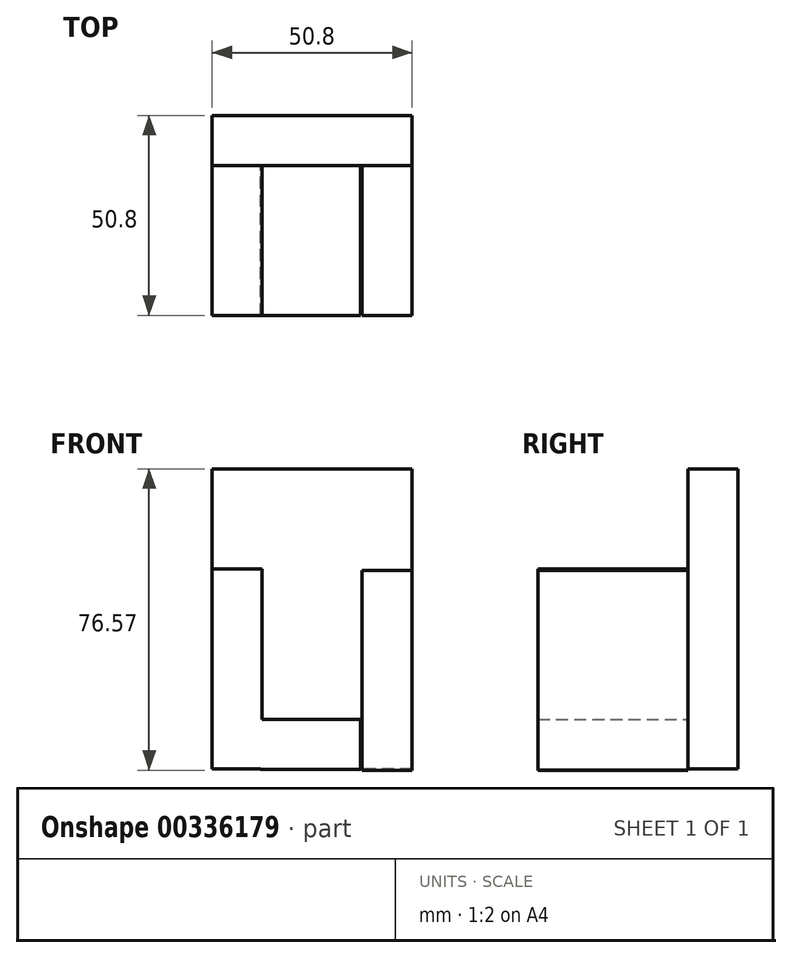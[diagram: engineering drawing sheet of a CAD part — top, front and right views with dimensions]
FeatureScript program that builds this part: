
annotation { "Feature Type Name" : "Feature", "Feature Type Description" : "" }
export const myFeature = defineFeature(function(context is Context, id is Id, definition is map)
    precondition{}
    {
        {
            var Q0;
            Q0=qCreatedBy(makeId("Right.planeOp"),FACE);
            var sketch = newSketch(context, id + "F0", { "sketchPlane" : qUnion([Q0])});
            skLineSegment(sketch, "E0.bottom", {"start": v(0, -25.4) * mm, "end": v(38.1, -25.4) * mm});
            skLineSegment(sketch, "E0.top", {"start": v(0, -76.2) * mm, "end": v(38.1, -76.2) * mm});
            skLineSegment(sketch, "E0.left", {"start": v(0, -25.4) * mm, "end": v(0, -76.2) * mm});
            skLineSegment(sketch, "E0.right", {"start": v(38.1, -25.4) * mm, "end": v(38.1, -76.2) * mm});
            skLineSegment(sketch, "E1.bottom", {"start": v(38.1, -76.2) * mm, "end": v(50.8, -76.2) * mm});
            skLineSegment(sketch, "E1.top", {"start": v(38.1, 0) * mm, "end": v(50.8, 0) * mm});
            skLineSegment(sketch, "E1.left", {"start": v(38.1, -76.2) * mm, "end": v(38.1, 0) * mm});
            skLineSegment(sketch, "E1.right", {"start": v(50.8, -76.2) * mm, "end": v(50.8, 0) * mm});
            skSolve(sketch);
        }
        {
            var Q0;
            {var subQ3=sQuery(id+"F0.wireOp",EDGE,"E1.bottom");Q0=makeQuery(id+"F0.imprint","IMPRINT",FACE,{"disambiguationData":[TD([[makeQuery(id+"F0.imprint","IMPRINT",EDGE,{"derivedFrom":subQ3}),1.0]])]});}
            extrude(context, id + "F1", {"entities" : qUnion([Q0]), "depth" : 50.8 * mm});
        }
        {
            var Q0;
            {var subQ0=sQuery(id+"F0.wireOp",EDGE,"E0.bottom");Q0=makeQuery(id+"F0.imprint","IMPRINT",FACE,{"disambiguationData":[TD([[makeQuery(id+"F0.imprint","IMPRINT",EDGE,{"derivedFrom":subQ0}),-1.0]])]});}
            extrude(context, id + "F2", {"entities" : qUnion([Q0]), "operationType" : NewBodyOperationType.ADD, "depth" : 12.7 * mm});
        }
        {
            var Q0;
            Q0=qCreatedBy(makeId("Front.planeOp"),FACE);
            var sketch = newSketch(context, id + "F3", { "sketchPlane" : qUnion([Q0])});
            skLineSegment(sketch, "E2.bottom", {"start": v(12.31, -76.42) * mm, "end": v(37.71, -76.42) * mm});
            skLineSegment(sketch, "E2.top", {"start": v(12.31, -63.72) * mm, "end": v(37.71, -63.72) * mm});
            skLineSegment(sketch, "E2.left", {"start": v(12.31, -76.42) * mm, "end": v(12.31, -63.72) * mm});
            skLineSegment(sketch, "E2.right", {"start": v(37.71, -76.42) * mm, "end": v(37.71, -63.72) * mm});
            skSolve(sketch);
        }
        {
            var Q0;
            Q0=makeQuery(id+"F3.imprint","IMPRINT",FACE,{"disambiguationData":[TD([[makeQuery(id+"F3.imprint","IMPRINT",EDGE,{"derivedFrom":sQuery(id+"F3.wireOp",EDGE,"E2.bottom")}),1.0]])]});
            extrude(context, id + "F4", {"entities" : qUnion([Q0]), "operationType" : NewBodyOperationType.ADD, "oppositeDirection" : true, "depth" : 38.1 * mm});
        }
        {
            var Q0;
            Q0=qCreatedBy(makeId("Front.planeOp"),FACE);
            var sketch = newSketch(context, id + "F5", { "sketchPlane" : qUnion([Q0])});
            skLineSegment(sketch, "E3.bottom", {"start": v(50.71, -76.57) * mm, "end": v(38.01, -76.57) * mm});
            skLineSegment(sketch, "E3.top", {"start": v(50.71, -25.77) * mm, "end": v(38.01, -25.77) * mm});
            skLineSegment(sketch, "E3.left", {"start": v(50.71, -76.57) * mm, "end": v(50.71, -25.77) * mm});
            skLineSegment(sketch, "E3.right", {"start": v(38.01, -76.57) * mm, "end": v(38.01, -25.77) * mm});
            skSolve(sketch);
        }
        {
            var Q0;
            Q0 = qSketchRegion(id + "F5", true);
            extrude(context, id + "F6", {"entities" : qUnion([Q0]), "operationType" : NewBodyOperationType.ADD, "oppositeDirection" : true, "depth" : 38.1 * mm});
        }
    });
